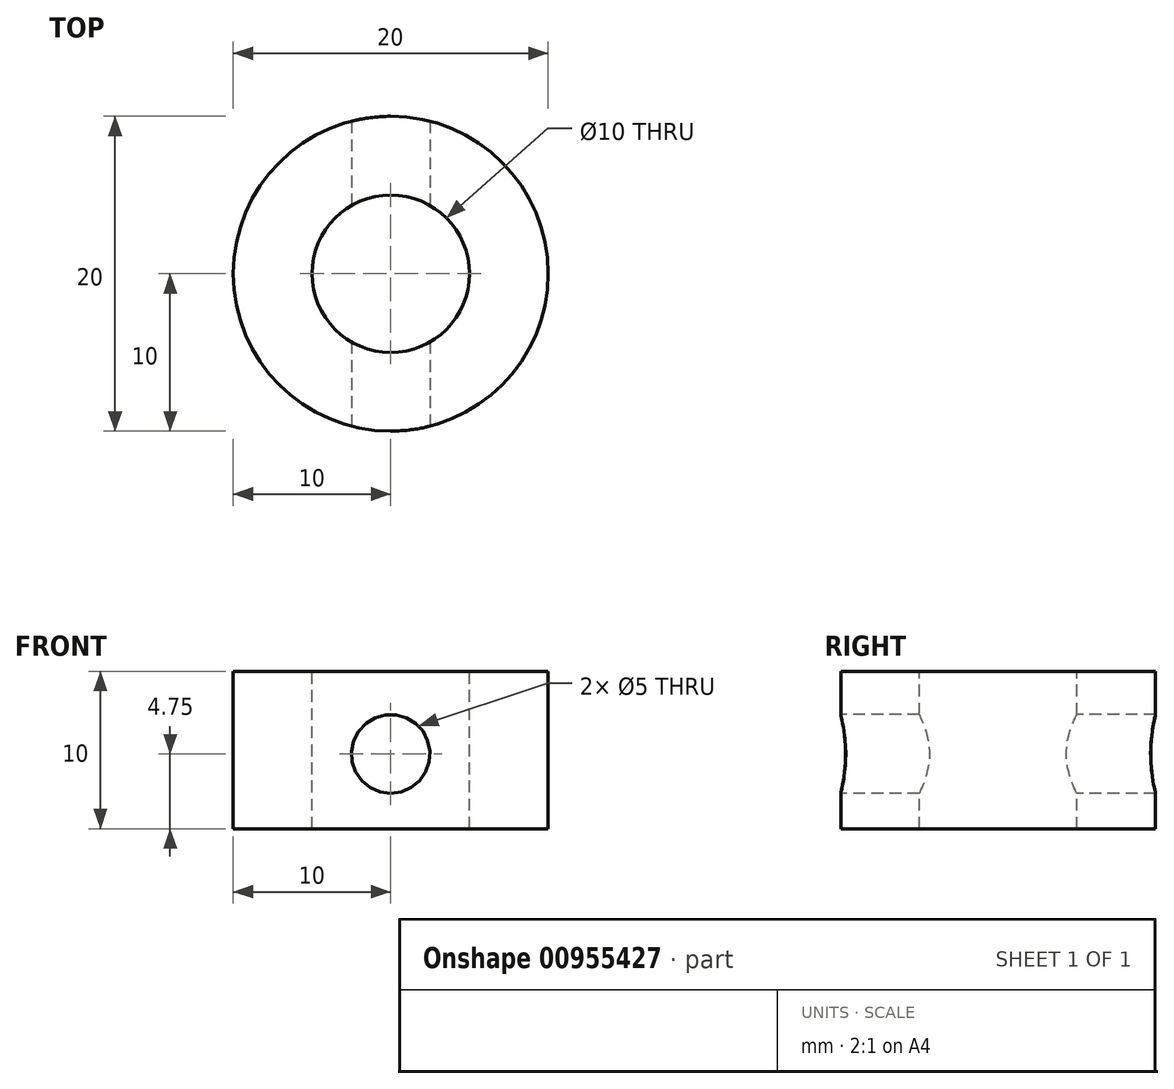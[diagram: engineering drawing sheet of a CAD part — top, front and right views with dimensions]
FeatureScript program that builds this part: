
annotation { "Feature Type Name" : "Feature", "Feature Type Description" : "" }
export const myFeature = defineFeature(function(context is Context, id is Id, definition is map)
    precondition{}
    {
        {
            var Q0;
            Q0=qCreatedBy(makeId("Top.planeOp"),FACE);
            var sketch = newSketch(context, id + "F0", { "sketchPlane" : qUnion([Q0])});
            skCircle(sketch, "E0", {"center": v(0, 0) * mm, "radius": 10 * mm});
            skSolve(sketch);
        }
        {
            var Q0;
            Q0 = qSketchRegion(id + "F0", true);
            extrude(context, id + "F1", {"entities" : qUnion([Q0]), "depth" : 10 * mm, "offsetDistance" : 25 * mm});
        }
        {
            var Q0;
            Q0=makeQuery(id+"F1.opExtrude","CAP_FACE",FACE,{"disambiguationData":[OSD([sQuery(id+"F0.wireOp",EDGE,"E0")])],"isStart":false});
            var sketch = newSketch(context, id + "F2", { "sketchPlane" : qUnion([Q0])});
            skCircle(sketch, "E1", {"center": v(0, 0) * mm, "radius": 5 * mm});
            skSolve(sketch);
        }
        {
            var Q0;
            Q0=makeQuery(id+"F2.imprint","IMPRINT",FACE,{"disambiguationData":[TD([[makeQuery(id+"F2.imprint","IMPRINT",EDGE,{"derivedFrom":sQuery(id+"F2.wireOp",EDGE,"E1")}),1.0]])]});
            extrude(context, id + "F3", {"entities" : qUnion([Q0]), "operationType" : NewBodyOperationType.REMOVE, "oppositeDirection" : true, "depth" : 25 * mm, "offsetDistance" : 25 * mm});
        }
        {
            var Q0;
            Q0=qCreatedBy(makeId("Front.planeOp"),FACE);
            var sketch = newSketch(context, id + "F4", { "sketchPlane" : qUnion([Q0])});
            skCircle(sketch, "E2", {"center": v(0, 4.75) * mm, "radius": 2.5 * mm});
            skSolve(sketch);
        }
        {
            var Q0;
            Q0 = qSketchRegion(id + "F4", true);
            extrude(context, id + "F5", {"entities" : qUnion([Q0]), "operationType" : NewBodyOperationType.REMOVE, "endBound" : BoundingType.SYMMETRIC, "oppositeDirection" : true, "depth" : 25 * mm, "offsetDistance" : 25 * mm});
        }
    });
